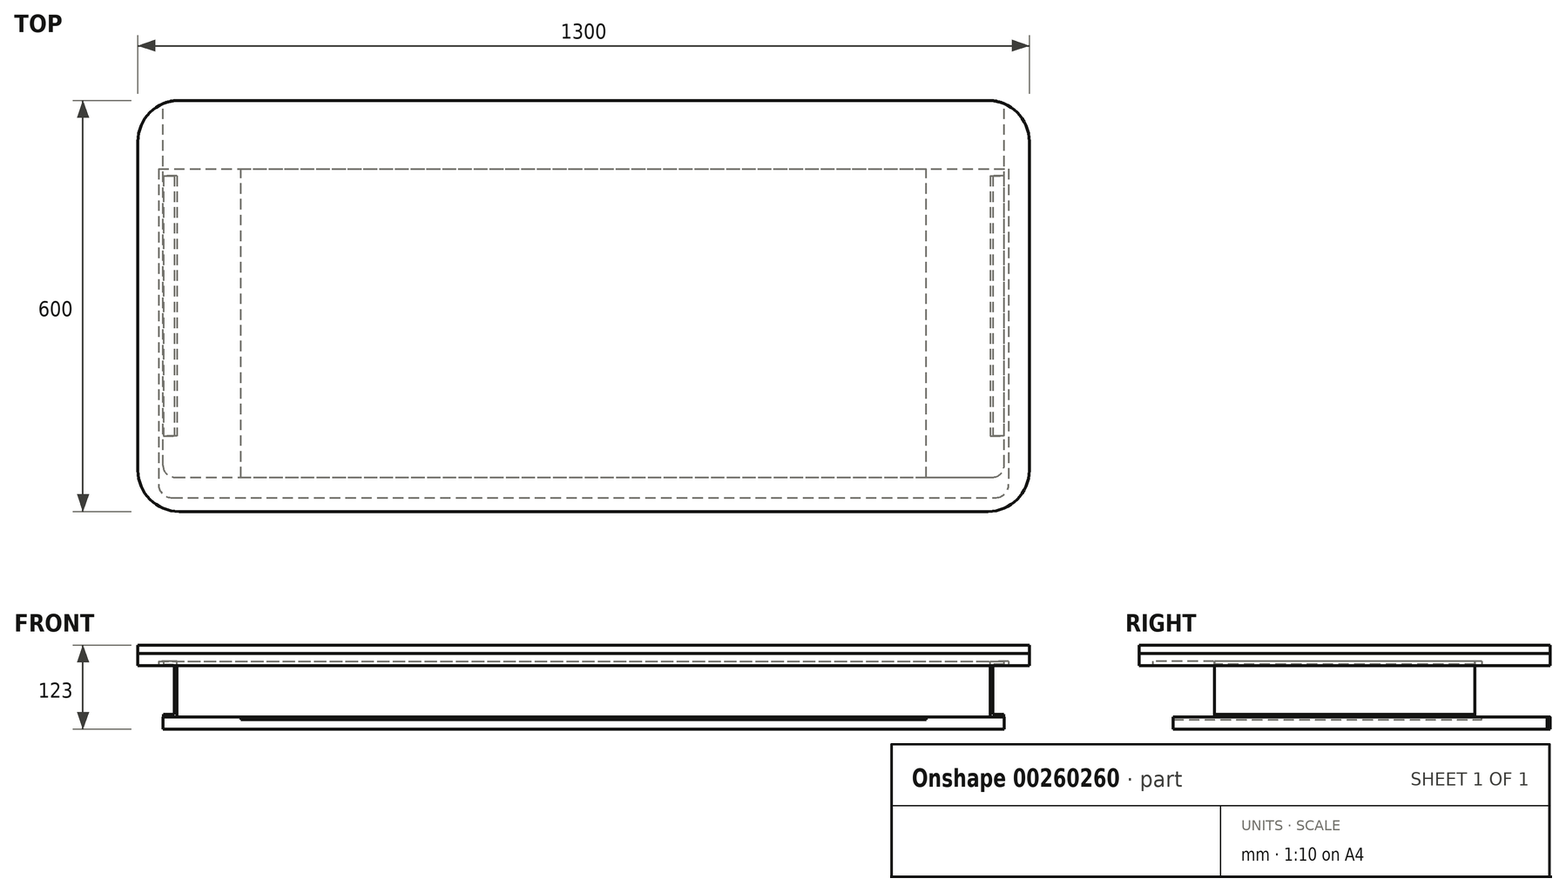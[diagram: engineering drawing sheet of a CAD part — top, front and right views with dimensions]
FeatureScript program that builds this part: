
annotation { "Feature Type Name" : "Feature", "Feature Type Description" : "" }
export const myFeature = defineFeature(function(context is Context, id is Id, definition is map)
    precondition{}
    {
        {
            var Q0;
            Q0=qCreatedBy(makeId("Top.planeOp"),FACE);
            var sketch = newSketch(context, id + "F0", { "sketchPlane" : qUnion([Q0])});
            skLineSegment(sketch, "E0.bottom", {"start": v(-590, 0) * mm, "end": v(590, 0) * mm});
            skLineSegment(sketch, "E0.top", {"start": v(-590, 600) * mm, "end": v(590, 600) * mm});
            skLineSegment(sketch, "E0.left", {"start": v(-650, 60) * mm, "end": v(-650, 540) * mm});
            skLineSegment(sketch, "E0.right", {"start": v(650, 60) * mm, "end": v(650, 540) * mm});
            skPoint(sketch, "E1.visualSharp", {"position": v(-650, 600) * mm});
            skArc(sketch, "E1.filletArc", {"start": v(-590, 600) * mm, "mid": v(-632.43, 582.43) * mm, "end": v(-650, 540) * mm});
            skPoint(sketch, "E2.visualSharp", {"position": v(-650, 0) * mm});
            skArc(sketch, "E2.filletArc", {"start": v(-650, 60) * mm, "mid": v(-632.43, 17.57) * mm, "end": v(-590, 0) * mm});
            skPoint(sketch, "E3.visualSharp", {"position": v(650, 600) * mm});
            skArc(sketch, "E3.filletArc", {"start": v(650, 540) * mm, "mid": v(632.43, 582.43) * mm, "end": v(590, 600) * mm});
            skPoint(sketch, "E4.visualSharp", {"position": v(650, 0) * mm});
            skArc(sketch, "E4.filletArc", {"start": v(590, 0) * mm, "mid": v(632.43, 17.57) * mm, "end": v(650, 60) * mm});
            skSolve(sketch);
        }
        {
            var Q0;
            Q0=makeQuery(id+"F0.imprint","IMPRINT",FACE,{"disambiguationData":[TD([[makeQuery(id+"F0.imprint","IMPRINT",EDGE,{"derivedFrom":sQuery(id+"F0.wireOp",EDGE,"E0.bottom")}),1.0]])]});
            extrude(context, id + "F1", {"entities" : qUnion([Q0]), "depth" : 12 * mm});
        }
        {
            var Q0;
            Q0=makeQuery(id+"F1.opExtrude","CAP_FACE",FACE,{"disambiguationData":[OSD([sQuery(id+"F0.wireOp",EDGE,"E0.bottom"),sQuery(id+"F0.wireOp",EDGE,"E0.top"),sQuery(id+"F0.wireOp",EDGE,"E0.left"),sQuery(id+"F0.wireOp",EDGE,"E0.right"),sQuery(id+"F0.wireOp",EDGE,"E1.filletArc"),sQuery(id+"F0.wireOp",EDGE,"E2.filletArc"),sQuery(id+"F0.wireOp",EDGE,"E3.filletArc"),sQuery(id+"F0.wireOp",EDGE,"E4.filletArc")])],"isStart":true});
            var sketch = newSketch(context, id + "F2", { "sketchPlane" : qUnion([Q0])});
            skLineSegment(sketch, "E5.0.0", {"start": v(-590, -600) * mm, "end": v(590, -600) * mm});
            skArc(sketch, "E5.0.1", {"start": v(590, -600) * mm, "mid": v(632.43, -582.43) * mm, "end": v(650, -540) * mm});
            skLineSegment(sketch, "E5.0.2", {"start": v(650, -540) * mm, "end": v(650, -60) * mm});
            skArc(sketch, "E5.0.3", {"start": v(650, -60) * mm, "mid": v(632.43, -17.57) * mm, "end": v(590, 0) * mm});
            skLineSegment(sketch, "E5.0.4", {"start": v(590, 0) * mm, "end": v(-590, 0) * mm});
            skArc(sketch, "E5.0.5", {"start": v(-590, 0) * mm, "mid": v(-632.43, -17.57) * mm, "end": v(-650, -60) * mm});
            skLineSegment(sketch, "E5.0.6", {"start": v(-650, -60) * mm, "end": v(-650, -540) * mm});
            skArc(sketch, "E5.0.7", {"start": v(-650, -540) * mm, "mid": v(-632.43, -582.43) * mm, "end": v(-590, -600) * mm});
            skSolve(sketch);
        }
        {
            var Q0;
            Q0 = qSketchRegion(id + "F2", true);
            extrude(context, id + "F3", {"entities" : qUnion([Q0]), "depth" : 18 * mm});
        }
        {
            var Q0;
            Q0=makeQuery(id+"F3.opExtrude","CAP_FACE",FACE,{"disambiguationData":[OSD([sQuery(id+"F2.wireOp",EDGE,"E5.0.0"),sQuery(id+"F2.wireOp",EDGE,"E5.0.1"),sQuery(id+"F2.wireOp",EDGE,"E5.0.2"),sQuery(id+"F2.wireOp",EDGE,"E5.0.3"),sQuery(id+"F2.wireOp",EDGE,"E5.0.4"),sQuery(id+"F2.wireOp",EDGE,"E5.0.5"),sQuery(id+"F2.wireOp",EDGE,"E5.0.6"),sQuery(id+"F2.wireOp",EDGE,"E5.0.7")])],"isStart":false});
            var sketch = newSketch(context, id + "F4", { "sketchPlane" : qUnion([Q0])});
            skLineSegment(sketch, "E6.bottom", {"start": v(-620, -500) * mm, "end": v(620, -500) * mm});
            skLineSegment(sketch, "E6.top", {"start": v(-620, -20) * mm, "end": v(620, -20) * mm});
            skLineSegment(sketch, "E6.left", {"start": v(-620, -500) * mm, "end": v(-620, -20) * mm});
            skLineSegment(sketch, "E6.right", {"start": v(620, -500) * mm, "end": v(620, -20) * mm});
            skSolve(sketch);
        }
        {
            var Q0;
            Q0=makeQuery(id+"F4.imprint","IMPRINT",FACE,{"disambiguationData":[TD([[makeQuery(id+"F4.imprint","IMPRINT",EDGE,{"derivedFrom":sQuery(id+"F4.wireOp",EDGE,"E6.bottom")}),1.0]])]});
            extrude(context, id + "F5", {"entities" : qUnion([Q0]), "operationType" : NewBodyOperationType.REMOVE, "oppositeDirection" : true, "depth" : 6 * mm});
        }
        {
            var Q0;
            Q0=makeQuery(id+"F5.boolean.opBoolean","COPY",EDGE,{"derivedFrom":makeQuery(id+"F5.opExtrude","SWEPT_EDGE",EDGE,{"disambiguationData":[OSD([sQuery(id+"F4.wireOp",EDGE,"E6.top"),sQuery(id+"F4.wireOp",EDGE,"E6.left")])]})});
            var Q1;
            Q1=makeQuery(id+"F5.boolean.opBoolean","COPY",EDGE,{"derivedFrom":makeQuery(id+"F5.opExtrude","SWEPT_EDGE",EDGE,{"disambiguationData":[OSD([sQuery(id+"F4.wireOp",EDGE,"E6.top"),sQuery(id+"F4.wireOp",EDGE,"E6.right")])]})});
            fillet(context, id + "F6", {"entities" : qUnion([Q0, Q1]), "radius" : 20 * mm, "tangentPropagation" : true, "allowEdgeOverflow" : false});
        }
        {
            var Q0;
            Q0=qCreatedBy(makeId("Front.planeOp"),FACE);
            cPlane(context, id + "F7", {"entities" : qUnion([Q0]), "cplaneType" : CPlaneType.OFFSET, "offset" : 110 * mm, "oppositeDirection" : true, "width" : 150 * mm, "height" : 150 * mm});
        }
        {
            var Q0;
            Q0=qCreatedBy(id+"F7.planeOp",FACE);
            var sketch = newSketch(context, id + "F8", { "sketchPlane" : qUnion([Q0])});
            skLineSegment(sketch, "E7", {"start": v(-613, -16) * mm, "end": v(-597, -16) * mm});
            skLineSegment(sketch, "E8", {"start": v(-597, -16) * mm, "end": v(-597, -89) * mm});
            skLineSegment(sketch, "E9", {"start": v(-597, -89) * mm, "end": v(-613, -89) * mm});
            skLineSegment(sketch, "E10", {"start": v(-613, -89) * mm, "end": v(-613, -93) * mm});
            skLineSegment(sketch, "E11", {"start": v(-613, -93) * mm, "end": v(-593, -93) * mm});
            skLineSegment(sketch, "E12", {"start": v(-593, -93) * mm, "end": v(-593, -12) * mm});
            skLineSegment(sketch, "E13", {"start": v(-593, -12) * mm, "end": v(-613, -12) * mm});
            skLineSegment(sketch, "E14", {"start": v(-613, -12) * mm, "end": v(-613, -16) * mm});
            skLineSegment(sketch, "E15", {"start": v(0, 0) * mm, "end": v(0, -13.76) * mm, "construction": true});
            skLineSegment(sketch, "E16", {"start": v(-597, -52.5) * mm, "end": v(-593, -52.5) * mm, "construction": true});
            skSolve(sketch);
        }
        {
            var Q0;
            Q0 = qSketchRegion(id + "F8", true);
            extrude(context, id + "F9", {"entities" : qUnion([Q0]), "oppositeDirection" : true, "depth" : 380 * mm});
        }
        {
            var Q0;
            Q0=makeQuery(id+"F9.opExtrude","SWEPT_BODY",BODY,{"disambiguationData":[OSD([sQuery(id+"F8.wireOp",EDGE,"E7"),sQuery(id+"F8.wireOp",EDGE,"E8"),sQuery(id+"F8.wireOp",EDGE,"E9"),sQuery(id+"F8.wireOp",EDGE,"E10"),sQuery(id+"F8.wireOp",EDGE,"E11"),sQuery(id+"F8.wireOp",EDGE,"E12"),sQuery(id+"F8.wireOp",EDGE,"E13"),sQuery(id+"F8.wireOp",EDGE,"E14")])]});
            var Q1;
            Q1=qCreatedBy(makeId("Right.planeOp"),FACE);
            mirror(context, id + "F10", {"operationType" : NewBodyOperationType.ADD, "entities" : qUnion([Q0]), "mirrorPlane" : qUnion([Q1])});
        }
        {
            var Q0;
            Q0=makeQuery(id+"F9.opExtrude","SWEPT_FACE",FACE,{"disambiguationData":[OSD([sQuery(id+"F8.wireOp",EDGE,"E11")])]});
            var sketch = newSketch(context, id + "F11", { "sketchPlane" : qUnion([Q0])});
            skLineSegment(sketch, "E17.bottom", {"start": v(-596.25, -50) * mm, "end": v(596.25, -50) * mm});
            skLineSegment(sketch, "E17.top", {"start": v(-590.25, -600) * mm, "end": v(590.25, -600) * mm});
            skLineSegment(sketch, "E17.left", {"start": v(-613.25, -67) * mm, "end": v(-613.25, -595.42) * mm});
            skLineSegment(sketch, "E17.right", {"start": v(613.25, -67) * mm, "end": v(613.25, -595.42) * mm});
            skPoint(sketch, "E18.visualSharp", {"position": v(-613.25, -50) * mm});
            skArc(sketch, "E18.filletArc", {"start": v(-596.25, -50) * mm, "mid": v(-608.27, -54.98) * mm, "end": v(-613.25, -67) * mm});
            skPoint(sketch, "E19.visualSharp", {"position": v(613.25, -50) * mm});
            skArc(sketch, "E19.filletArc", {"start": v(613.25, -67) * mm, "mid": v(608.27, -54.98) * mm, "end": v(596.25, -50) * mm});
            skLineSegment(sketch, "E20", {"start": v(0, -600) * mm, "end": v(0, -50) * mm, "construction": true});
            skArc(sketch, "E21", {"start": v(-613.25, -595.42) * mm, "mid": v(-601.98, -598.84) * mm, "end": v(-590.25, -600) * mm});
            skArc(sketch, "E22", {"start": v(590.25, -600) * mm, "mid": v(601.98, -598.84) * mm, "end": v(613.25, -595.42) * mm});
            skPoint(sketch, "E23.orphan", {"position": v(-613.25, -600) * mm});
            skPoint(sketch, "E24.orphan", {"position": v(613.25, -600) * mm});
            skSolve(sketch);
        }
        {
            var Q0;
            Q0 = qSketchRegion(id + "F11", true);
            extrude(context, id + "F12", {"entities" : qUnion([Q0]), "depth" : 18 * mm});
        }
        {
            var Q0;
            Q0=makeQuery(id+"F12.opExtrude","CAP_FACE",FACE,{"disambiguationData":[OSD([sQuery(id+"F11.wireOp",EDGE,"E17.bottom"),sQuery(id+"F11.wireOp",EDGE,"E17.top"),sQuery(id+"F11.wireOp",EDGE,"E17.left"),sQuery(id+"F11.wireOp",EDGE,"E17.right"),sQuery(id+"F11.wireOp",EDGE,"E18.filletArc"),sQuery(id+"F11.wireOp",EDGE,"E19.filletArc"),sQuery(id+"F11.wireOp",EDGE,"E21"),sQuery(id+"F11.wireOp",EDGE,"E22")])],"isStart":true});
            var sketch = newSketch(context, id + "F13", { "sketchPlane" : qUnion([Q0])});
            skLineSegment(sketch, "E25.bottom", {"start": v(-500, 50) * mm, "end": v(500, 50) * mm});
            skLineSegment(sketch, "E25.top", {"start": v(-500, 500) * mm, "end": v(500, 500) * mm});
            skLineSegment(sketch, "E25.left", {"start": v(-500, 50) * mm, "end": v(-500, 500) * mm});
            skLineSegment(sketch, "E25.right", {"start": v(500, 50) * mm, "end": v(500, 500) * mm});
            skLineSegment(sketch, "E26", {"start": v(0, 500) * mm, "end": v(0, 50) * mm, "construction": true});
            skSolve(sketch);
        }
        {
            var Q0;
            Q0=makeQuery(id+"F13.imprint","IMPRINT",FACE,{"disambiguationData":[TD([[makeQuery(id+"F13.imprint","IMPRINT",EDGE,{"derivedFrom":sQuery(id+"F13.wireOp",EDGE,"E25.bottom")}),1.0]])]});
            var Q1;
            Q1=sQuery(id+"F13.wireOp",EDGE,"E25.left");
            var Q2;
            Q2=sQuery(id+"F13.wireOp",EDGE,"E25.top");
            var Q3;
            Q3=sQuery(id+"F13.wireOp",EDGE,"E25.bottom");
            var Q4;
            Q4=sQuery(id+"F13.wireOp",EDGE,"E25.right");
            extrude(context, id + "F14", {"entities" : qUnion([Q0]), "operationType" : NewBodyOperationType.REMOVE, "surfaceEntities" : qUnion([Q1, Q2, Q3, Q4]), "oppositeDirection" : true, "depth" : 4 * mm});
        }
    });
